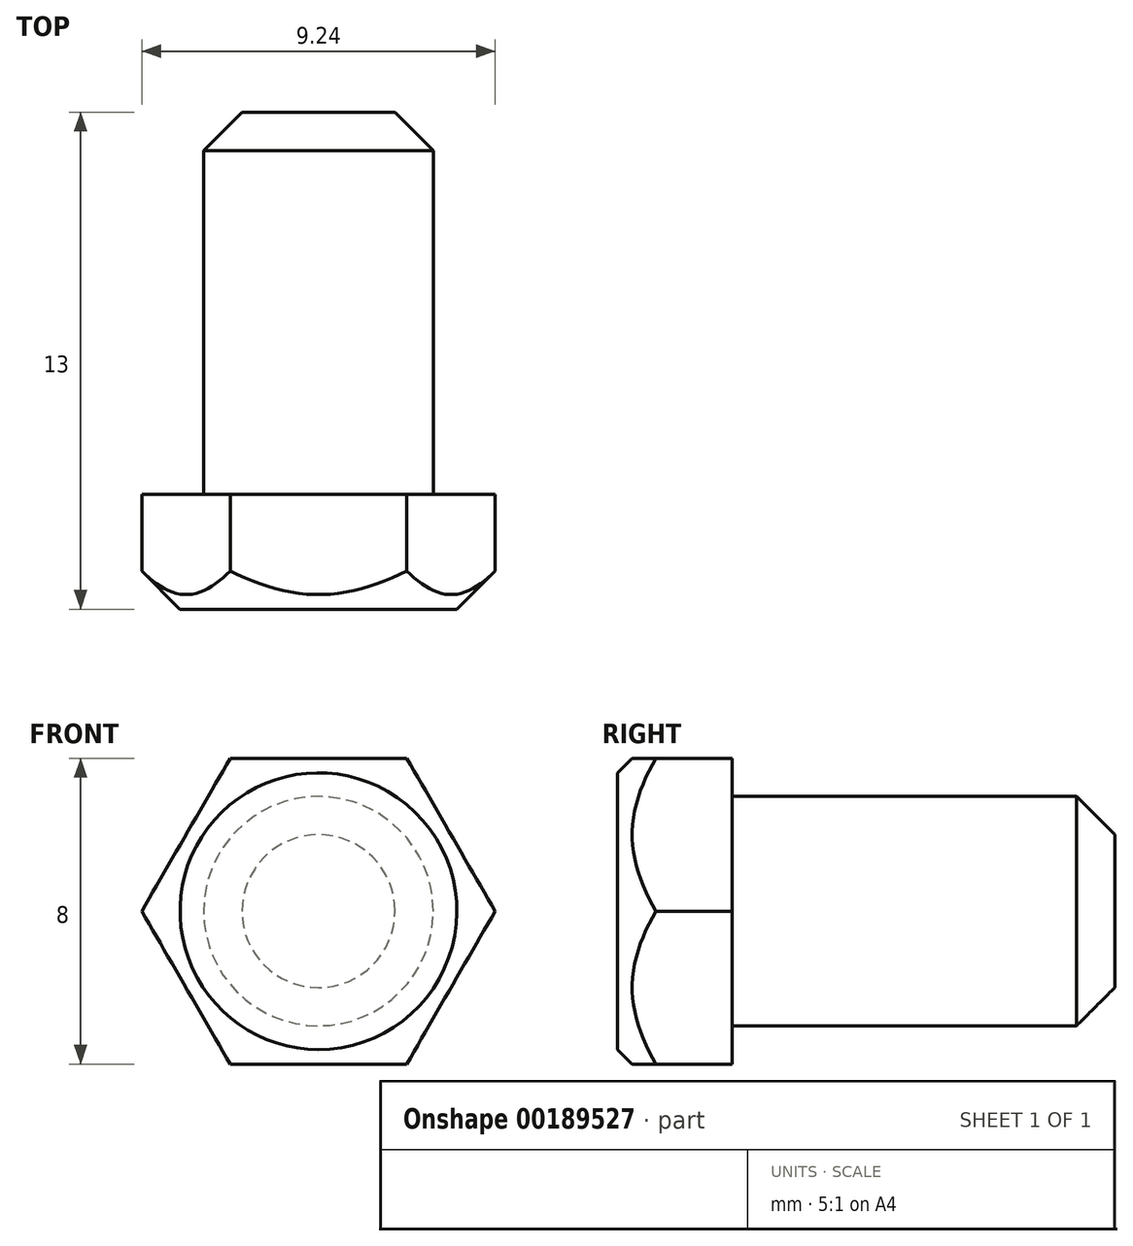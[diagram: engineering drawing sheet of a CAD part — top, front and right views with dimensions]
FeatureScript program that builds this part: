
annotation { "Feature Type Name" : "Feature", "Feature Type Description" : "" }
export const myFeature = defineFeature(function(context is Context, id is Id, definition is map)
    precondition{}
    {
        {
            var Q0;
            Q0=qCreatedBy(makeId("Front.planeOp"),FACE);
            var sketch = newSketch(context, id + "F0", { "sketchPlane" : qUnion([Q0])});
            skCircle(sketch, "E0.cCircle", {"center": v(0, 0) * mm, "radius": 4 * mm, "construction": true});
            skLineSegment(sketch, "E0.0", {"start": v(-2.3, 4) * mm, "end": v(2.3, 4) * mm});
            skLineSegment(sketch, "E0.1", {"start": v(2.3, 4) * mm, "end": v(4.62, 0) * mm});
            skLineSegment(sketch, "E0.2", {"start": v(4.62, 0) * mm, "end": v(2.3, -4) * mm});
            skLineSegment(sketch, "E0.3", {"start": v(2.3, -4) * mm, "end": v(-2.3, -4) * mm});
            skLineSegment(sketch, "E0.4", {"start": v(-2.3, -4) * mm, "end": v(-4.62, 0) * mm});
            skLineSegment(sketch, "E0.5", {"start": v(-4.62, 0) * mm, "end": v(-2.3, 4) * mm});
            skPoint(sketch, "E0.0.midPoint", {"position": v(0, 4) * mm});
            skCircle(sketch, "E1", {"center": v(0, 0) * mm, "radius": 3 * mm});
            skCircle(sketch, "E2", {"center": v(0, 0) * mm, "radius": 4.62 * mm});
            skSolve(sketch);
        }
        {
            var Q0;
            Q0 = qSketchRegion(id + "F0", true);
            var Q1;
            Q1=makeQuery(id+"F0.imprint","IMPRINT",FACE,{"disambiguationData":[TD([[makeQuery(id+"F0.imprint","IMPRINT",EDGE,{"derivedFrom":sQuery(id+"F0.wireOp",EDGE,"E1")}),1.0]])]});
            extrude(context, id + "F1", {"entities" : qUnion([Q0, Q1]), "depth" : 3 * mm});
        }
        {
            var Q0;
            Q0=makeQuery(id+"F1.opExtrude","CAP_EDGE",EDGE,{"disambiguationData":[OSD([sQuery(id+"F0.wireOp",EDGE,"E2")])],"isStart":false});
            chamfer(context, id + "F2", {"entities" : qUnion([Q0]), "width" : 1 * mm, "tangentPropagation" : true});
        }
        {
            var Q0;
            Q0=makeQuery(id+"F0.imprint","IMPRINT",FACE,{"disambiguationData":[TD([[makeQuery(id+"F0.imprint","IMPRINT",EDGE,{"derivedFrom":sQuery(id+"F0.wireOp",EDGE,"E0.0")}),-1.0]])]});
            var Q1;
            Q1=makeQuery(id+"F0.imprint","IMPRINT",FACE,{"disambiguationData":[TD([[makeQuery(id+"F0.imprint","IMPRINT",EDGE,{"derivedFrom":sQuery(id+"F0.wireOp",EDGE,"E1")}),1.0]])]});
            extrude(context, id + "F3", {"entities" : qUnion([Q0, Q1]), "operationType" : NewBodyOperationType.INTERSECT, "depth" : 25 * mm});
        }
        {
            var Q0;
            Q0=makeQuery(id+"F0.imprint","IMPRINT",FACE,{"disambiguationData":[TD([[makeQuery(id+"F0.imprint","IMPRINT",EDGE,{"derivedFrom":sQuery(id+"F0.wireOp",EDGE,"E1")}),1.0]])]});
            extrude(context, id + "F4", {"entities" : qUnion([Q0]), "operationType" : NewBodyOperationType.ADD, "oppositeDirection" : true, "depth" : 10 * mm});
        }
        {
            var Q0;
            Q0=makeQuery(id+"F4.opExtrude","CAP_EDGE",EDGE,{"disambiguationData":[OSD([sQuery(id+"F0.wireOp",EDGE,"E1")])],"isStart":false});
            chamfer(context, id + "F5", {"entities" : qUnion([Q0]), "width" : 1 * mm, "tangentPropagation" : true});
        }
    });
